# Revit family: Toilet_Seat-Elongated_Closed_Front-KOHLER-C3-230-K-76421BR
name_source: partatom
category: Plumbing Fixtures
revit_build: Autodesk Revit 2017 (Build: 20160225_1515(x64)
units: mm (PartAtom-declared; Revit-internal decimal feet)

## family parameters
Cut with Voids When Loaded = No
Host = Face
OmniClass Number = 23.31.25.00
OmniClass Title = Toilet and Bath Specialties
Part Type = Normal
Room Calculation Point = No
Round Connector Dimension = Use Diameter
Shared = No

## types (1)
- 0-White
    ADA Compliant = No
    Apparent Load = 0 VA
    Assembly Code = C1030200
    CW Connection = Yes
    Cold Water Inlet = Cold Water Inlet
    Date Modified = 01/27/2020
    Default Elevation = 0"
    Description = Electronic toilet seat with -220V bidet function
    Electrical Connector = Yes
    Electrical Note = Requires a dedicated circuit, protected by a power switch
Class A ground fault circuit (GFCI) or
residual current device (RCD)
    Finish = Kohler-Plastic-0-White
    Height = 6 1/16"
    Length = 20 7/16"
    Manufacturer = KOHLER Co.
    MasterFormat 1995 = 10820
    MasterFormat 2004 = 10.28.13
    Material = Plastic
    Model = K-76421BR
    Product Documentation Link = http://resources.kohler.com
    Product Name = C3 -230
    Product Page URL = https://br.kohler.com
    Type = 1
    URL = https://br.kohler.com
    Voltage = 220 V
    Width = 17 1/8"

## geometry (parser evidence)
native form markers: Sweep x6
no freeform markers — native parametric forms only
